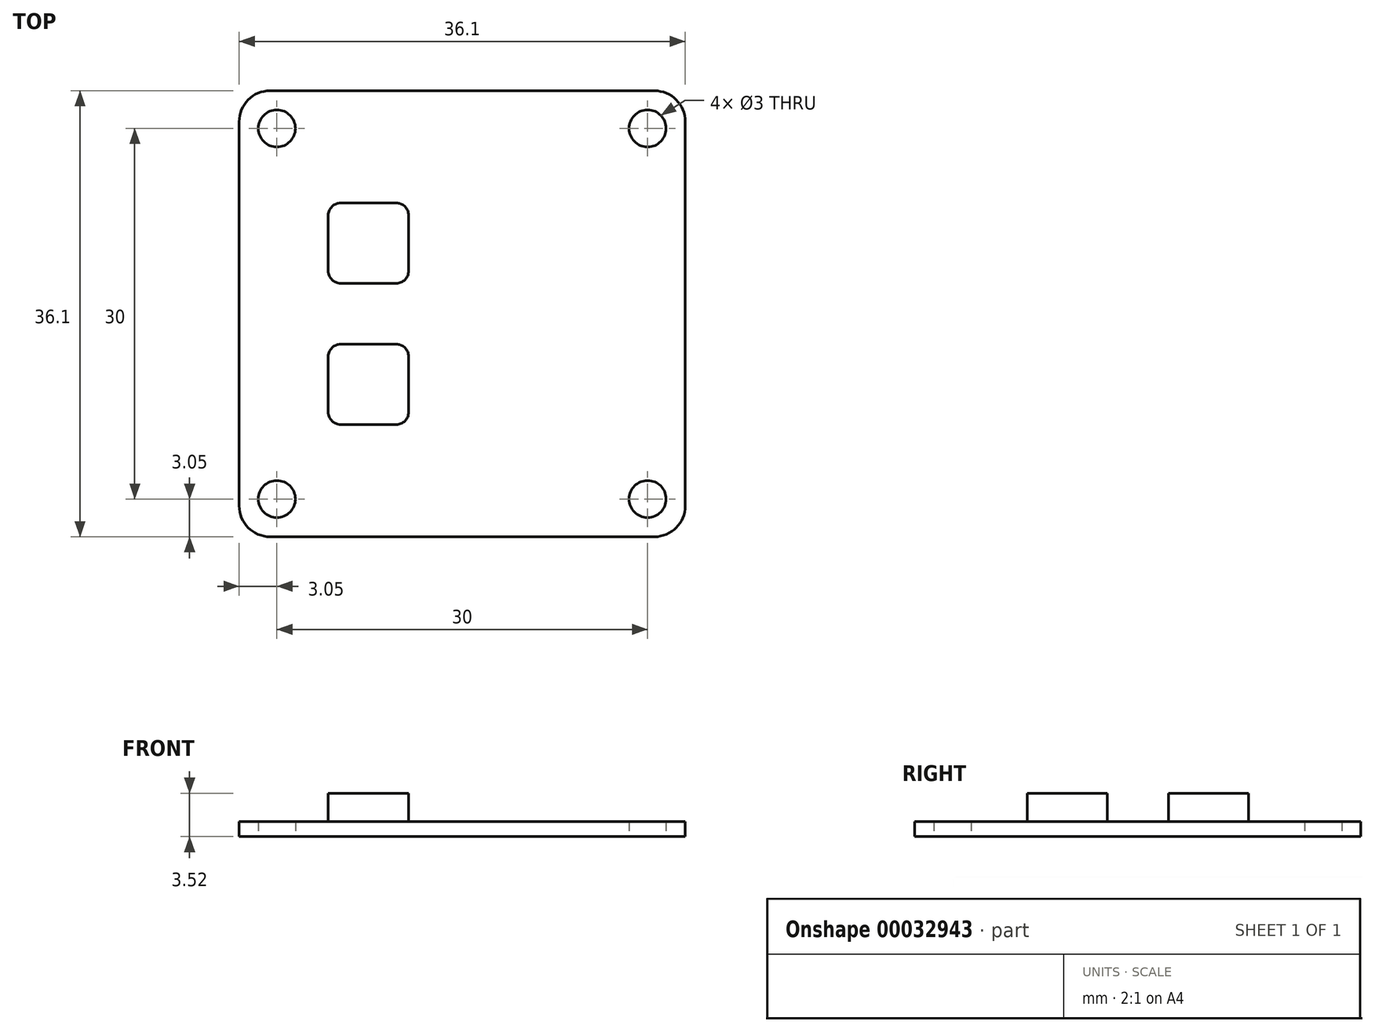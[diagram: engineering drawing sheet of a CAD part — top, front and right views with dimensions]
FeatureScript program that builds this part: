
annotation { "Feature Type Name" : "Feature", "Feature Type Description" : "" }
export const myFeature = defineFeature(function(context is Context, id is Id, definition is map)
    precondition{}
    {
        {
            var Q0;
            Q0=qCreatedBy(makeId("Top.planeOp"),FACE);
            var sketch = newSketch(context, id + "F0", { "sketchPlane" : qUnion([Q0])});
            skLineSegment(sketch, "E0.rect.bottom", {"start": v(18.05, -18.05) * mm, "end": v(-18.05, -18.05) * mm});
            skLineSegment(sketch, "E0.rect.top", {"start": v(18.05, 18.05) * mm, "end": v(-18.05, 18.05) * mm});
            skLineSegment(sketch, "E0.rect.left", {"start": v(18.05, -18.05) * mm, "end": v(18.05, 18.05) * mm});
            skLineSegment(sketch, "E0.rect.right", {"start": v(-18.05, -18.05) * mm, "end": v(-18.05, 18.05) * mm});
            skPoint(sketch, "E0.rect.middle", {"position": v(0, 0) * mm});
            skLineSegment(sketch, "E1.rect.bottom", {"start": v(15, -15) * mm, "end": v(-15, -15) * mm, "construction": true});
            skLineSegment(sketch, "E1.rect.top", {"start": v(15, 15) * mm, "end": v(-15, 15) * mm, "construction": true});
            skLineSegment(sketch, "E1.rect.left", {"start": v(15, -15) * mm, "end": v(15, 15) * mm, "construction": true});
            skLineSegment(sketch, "E1.rect.right", {"start": v(-15, -15) * mm, "end": v(-15, 15) * mm, "construction": true});
            skCircle(sketch, "E2", {"center": v(15, 15) * mm, "radius": 1.5 * mm});
            skCircle(sketch, "E3.1.0", {"center": v(-15, 15) * mm, "radius": 1.5 * mm});
            skCircle(sketch, "E3.2.0", {"center": v(-15, -15) * mm, "radius": 1.5 * mm});
            skCircle(sketch, "E3.3.0", {"center": v(15, -15) * mm, "radius": 1.5 * mm});
            skSolve(sketch);
        }
        {
            var Q0;
            Q0 = qSketchRegion(id + "F0", true);
            extrude(context, id + "F1", {"entities" : qUnion([Q0]), "depth" : 1.22 * mm});
        }
        {
            var Q0;
            Q0=makeQuery(id+"F1.opExtrude","SWEPT_EDGE",EDGE,{"disambiguationData":[OSD([sQuery(id+"F0.wireOp",EDGE,"E0.rect.top"),sQuery(id+"F0.wireOp",EDGE,"E0.rect.left")])]});
            var Q1;
            Q1=makeQuery(id+"F1.opExtrude","SWEPT_EDGE",EDGE,{"disambiguationData":[OSD([sQuery(id+"F0.wireOp",EDGE,"E0.rect.bottom"),sQuery(id+"F0.wireOp",EDGE,"E0.rect.left")])]});
            var Q2;
            Q2=makeQuery(id+"F1.opExtrude","SWEPT_EDGE",EDGE,{"disambiguationData":[OSD([sQuery(id+"F0.wireOp",EDGE,"E0.rect.bottom"),sQuery(id+"F0.wireOp",EDGE,"E0.rect.right")])]});
            var Q3;
            Q3=makeQuery(id+"F1.opExtrude","SWEPT_EDGE",EDGE,{"disambiguationData":[OSD([sQuery(id+"F0.wireOp",EDGE,"E0.rect.top"),sQuery(id+"F0.wireOp",EDGE,"E0.rect.right")])]});
            fillet(context, id + "F2", {"entities" : qUnion([Q0, Q1, Q2, Q3]), "radius" : 2.5 * mm, "tangentPropagation" : true, "allowEdgeOverflow" : false});
        }
        {
            var Q0;
            Q0=makeQuery(id+"F1.opExtrude","CAP_FACE",FACE,{"disambiguationData":[OSD([sQuery(id+"F0.wireOp",EDGE,"E0.rect.bottom"),sQuery(id+"F0.wireOp",EDGE,"E0.rect.top"),sQuery(id+"F0.wireOp",EDGE,"E0.rect.left"),sQuery(id+"F0.wireOp",EDGE,"E0.rect.right"),sQuery(id+"F0.wireOp",EDGE,"E2"),sQuery(id+"F0.wireOp",EDGE,"E3.1.0"),sQuery(id+"F0.wireOp",EDGE,"E3.2.0"),sQuery(id+"F0.wireOp",EDGE,"E3.3.0")])],"isStart":false});
            var sketch = newSketch(context, id + "F3", { "sketchPlane" : qUnion([Q0])});
            skLineSegment(sketch, "E4.rect.bottom", {"start": v(-10.84, -2.46) * mm, "end": v(-4.34, -2.46) * mm});
            skLineSegment(sketch, "E4.rect.top", {"start": v(-10.84, -8.96) * mm, "end": v(-4.34, -8.96) * mm});
            skLineSegment(sketch, "E4.rect.left", {"start": v(-10.84, -2.46) * mm, "end": v(-10.84, -8.96) * mm});
            skLineSegment(sketch, "E4.rect.right", {"start": v(-4.34, -2.46) * mm, "end": v(-4.34, -8.96) * mm});
            skPoint(sketch, "E4.rect.middle", {"position": v(-7.59, -5.71) * mm});
            skLineSegment(sketch, "E5.MirrorCS", {"start": v(-10.84, 2.46) * mm, "end": v(-4.34, 2.46) * mm});
            skLineSegment(sketch, "E6.MirrorCS", {"start": v(-4.34, 2.46) * mm, "end": v(-4.34, 8.96) * mm});
            skLineSegment(sketch, "E7.MirrorCS", {"start": v(-10.84, 8.96) * mm, "end": v(-4.34, 8.96) * mm});
            skLineSegment(sketch, "E8.MirrorCS", {"start": v(-10.84, 2.46) * mm, "end": v(-10.84, 8.96) * mm});
            skSolve(sketch);
        }
        {
            var Q0;
            Q0 = qSketchRegion(id + "F3", true);
            extrude(context, id + "F4", {"entities" : qUnion([Q0]), "operationType" : NewBodyOperationType.ADD, "depth" : 2.3 * mm});
        }
        {
            var Q0;
            Q0=makeQuery(id+"F4.opExtrude","SWEPT_EDGE",EDGE,{"disambiguationData":[OSD([sQuery(id+"F3.wireOp",EDGE,"E4.rect.top"),sQuery(id+"F3.wireOp",EDGE,"E4.rect.left")])]});
            var Q1;
            Q1=makeQuery(id+"F4.opExtrude","SWEPT_EDGE",EDGE,{"disambiguationData":[OSD([sQuery(id+"F3.wireOp",EDGE,"E4.rect.top"),sQuery(id+"F3.wireOp",EDGE,"E4.rect.right")])]});
            var Q2;
            Q2=makeQuery(id+"F4.opExtrude","SWEPT_EDGE",EDGE,{"disambiguationData":[OSD([sQuery(id+"F3.wireOp",EDGE,"E4.rect.bottom"),sQuery(id+"F3.wireOp",EDGE,"E4.rect.right")])]});
            var Q3;
            Q3=makeQuery(id+"F4.opExtrude","SWEPT_EDGE",EDGE,{"disambiguationData":[OSD([sQuery(id+"F3.wireOp",EDGE,"E4.rect.bottom"),sQuery(id+"F3.wireOp",EDGE,"E4.rect.left")])]});
            var Q4;
            Q4=makeQuery(id+"F4.opExtrude","SWEPT_EDGE",EDGE,{"disambiguationData":[OSD([sQuery(id+"F3.wireOp",EDGE,"E7.MirrorCS"),sQuery(id+"F3.wireOp",EDGE,"E8.MirrorCS")])]});
            var Q5;
            Q5=makeQuery(id+"F4.opExtrude","SWEPT_EDGE",EDGE,{"disambiguationData":[OSD([sQuery(id+"F3.wireOp",EDGE,"E5.MirrorCS"),sQuery(id+"F3.wireOp",EDGE,"E8.MirrorCS")])]});
            var Q6;
            Q6=makeQuery(id+"F4.opExtrude","SWEPT_EDGE",EDGE,{"disambiguationData":[OSD([sQuery(id+"F3.wireOp",EDGE,"E6.MirrorCS"),sQuery(id+"F3.wireOp",EDGE,"E7.MirrorCS")])]});
            var Q7;
            Q7=makeQuery(id+"F4.opExtrude","SWEPT_EDGE",EDGE,{"disambiguationData":[OSD([sQuery(id+"F3.wireOp",EDGE,"E5.MirrorCS"),sQuery(id+"F3.wireOp",EDGE,"E6.MirrorCS")])]});
            fillet(context, id + "F5", {"entities" : qUnion([Q0, Q1, Q2, Q3, Q4, Q5, Q6, Q7]), "radius" : 1 * mm, "tangentPropagation" : true, "allowEdgeOverflow" : false});
        }
    });
